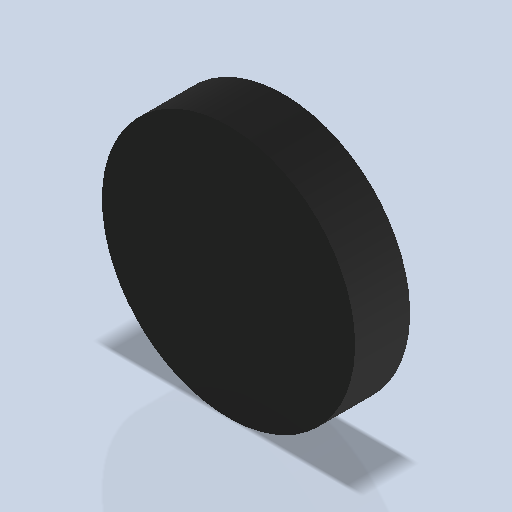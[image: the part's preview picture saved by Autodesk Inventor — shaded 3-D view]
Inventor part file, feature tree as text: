
AUTODESK INVENTOR PART (.ipt)
format: ipt  version: 2024.2 (Build 282272000, 272)  size: 214,016 bytes
history: native  units: mm
features: extrude x2, sketch x2
ambient origin geometry x8: Origin, YZ Plane, XZ Plane, XY Plane, X Axis, Y Axis, Z Axis, Center Point
bodies: Volumenkörper1 (feature_tree)
feature tree (4):
  extrude  "Extrusion1"  Depth=20.0mm TaperAngle=0.0deg
  extrude  "Extrusion2"  Depth=10.0mm TaperAngle=0.0deg
  sketch  "Skizze1"  dims[d0=92.0mm d1=20.0mm d2=0.0mm]
  sketch  "Skizze2"  dims[d3=30.0mm d4=10.0mm d5=0.0mm]
